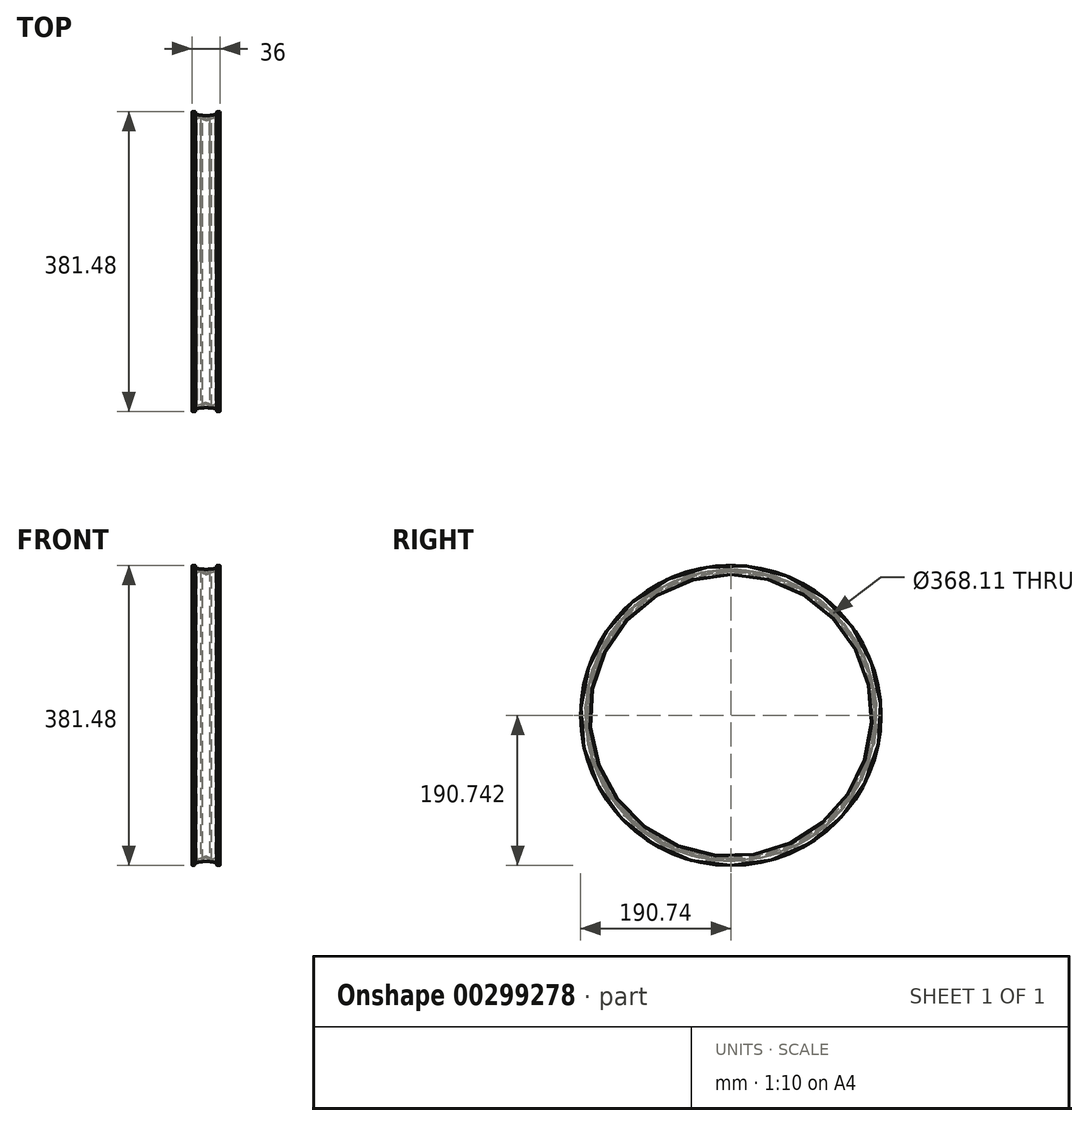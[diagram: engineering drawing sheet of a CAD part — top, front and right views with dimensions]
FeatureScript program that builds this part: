
annotation { "Feature Type Name" : "Feature", "Feature Type Description" : "" }
export const myFeature = defineFeature(function(context is Context, id is Id, definition is map)
    precondition{}
    {
        {
            var Q0;
            Q0=qCreatedBy(makeId("Front.planeOp"),FACE);
            var sketch = newSketch(context, id + "F0", { "sketchPlane" : qUnion([Q0])});
            skLineSegment(sketch, "E0", {"start": v(-18, 0) * mm, "end": v(-18, 12) * mm});
            skPoint(sketch, "E1", {"position": v(-14.7, 0) * mm});
            skPoint(sketch, "E2", {"position": v(-14.7, 2.3) * mm});
            skArc(sketch, "E3", {"start": v(-14.7, 0) * mm, "mid": v(-13.4, 1.15) * mm, "end": v(-14.7, 2.3) * mm});
            skLineSegment(sketch, "E4", {"start": v(-14.7, 2.3) * mm, "end": v(-14.7, 3.3) * mm});
            skLineSegment(sketch, "E5", {"start": v(-18, 12) * mm, "end": v(-9, 8.18) * mm});
            skLineSegment(sketch, "E6", {"start": v(-9, 8.18) * mm, "end": v(0, 12) * mm});
            skPoint(sketch, "E7", {"position": v(-14.7, 4.05) * mm});
            skLineSegment(sketch, "E8", {"start": v(-14.7, 4.05) * mm, "end": v(-14.7, 5.73) * mm});
            skLineSegment(sketch, "E9", {"start": v(-14.7, 5.73) * mm, "end": v(-0.65, 5.73) * mm});
            skLineSegment(sketch, "E10", {"start": v(-0.65, 5.73) * mm, "end": v(-14.7, 4.05) * mm});
            skPoint(sketch, "E11", {"position": v(0, 5.73) * mm});
            skLineSegment(sketch, "E12", {"start": v(-14.7, 6.73) * mm, "end": v(-14.7, 8.43) * mm});
            skLineSegment(sketch, "E13", {"start": v(-14.7, 8.43) * mm, "end": v(-10.58, 6.68) * mm});
            skLineSegment(sketch, "E14", {"start": v(-14.7, 6.73) * mm, "end": v(-10.58, 6.68) * mm});
            skPoint(sketch, "E15", {"position": v(0, 9.94) * mm});
            skLineSegment(sketch, "E16", {"start": v(0, 9.94) * mm, "end": v(-7.68, 6.68) * mm});
            skLineSegment(sketch, "E17", {"start": v(-7.68, 6.68) * mm, "end": v(0, 6.68) * mm});
            skLineSegment(sketch, "E18.MirrorCS", {"start": v(9, 8.18) * mm, "end": v(0, 12) * mm});
            skLineSegment(sketch, "E19.MirrorCS", {"start": v(0, 9.94) * mm, "end": v(7.68, 6.68) * mm});
            skLineSegment(sketch, "E20.MirrorCS", {"start": v(7.68, 6.68) * mm, "end": v(0, 6.68) * mm});
            skLineSegment(sketch, "E21.MirrorCS", {"start": v(0.65, 5.73) * mm, "end": v(14.7, 4.05) * mm});
            skLineSegment(sketch, "E22.MirrorCS", {"start": v(14.7, 4.05) * mm, "end": v(14.7, 5.73) * mm});
            skLineSegment(sketch, "E23.MirrorCS", {"start": v(18, 0) * mm, "end": v(18, 12) * mm});
            skArc(sketch, "E24.MirrorCS", {"start": v(14.7, 0) * mm, "mid": v(13.41, 1.15) * mm, "end": v(14.7, 2.3) * mm});
            skLineSegment(sketch, "E25.MirrorCS", {"start": v(14.7, 2.3) * mm, "end": v(14.7, 3.3) * mm});
            skLineSegment(sketch, "E26.MirrorCS", {"start": v(18, 12) * mm, "end": v(9, 8.18) * mm});
            skLineSegment(sketch, "E27", {"start": v(-18, 0) * mm, "end": v(-14.7, 0) * mm});
            skLineSegment(sketch, "E28", {"start": v(18, 0) * mm, "end": v(14.7, 0) * mm});
            skLineSegment(sketch, "E29.MirrorCS", {"start": v(14.7, 6.73) * mm, "end": v(10.58, 6.68) * mm});
            skLineSegment(sketch, "E30.MirrorCS", {"start": v(14.7, 6.73) * mm, "end": v(14.7, 8.43) * mm});
            skLineSegment(sketch, "E31.MirrorCS", {"start": v(14.7, 8.43) * mm, "end": v(10.58, 6.68) * mm});
            skArc(sketch, "E32", {"start": v(14.7, 3.3) * mm, "mid": v(0, 5.1) * mm, "end": v(-14.7, 3.3) * mm});
            skPoint(sketch, "E33", {"position": v(0, 2.3) * mm});
            skLineSegment(sketch, "E34", {"start": v(0, 2.3) * mm, "end": v(0, 190.73) * mm, "construction": true});
            skLineSegment(sketch, "E35", {"start": v(0, 190.73) * mm, "end": v(86.7, 190.73) * mm, "construction": true});
            skLineSegment(sketch, "E36", {"start": v(0.65, 5.73) * mm, "end": v(14.7, 5.73) * mm});
            skSolve(sketch);
        }
        {
            var Q0;
            Q0=makeQuery(id+"F0.imprint","IMPRINT",FACE,{"disambiguationData":[TD([[makeQuery(id+"F0.imprint","IMPRINT",EDGE,{"derivedFrom":sQuery(id+"F0.wireOp",EDGE,"E0")}),-1.0]])]});
            var Q1;
            Q1=sQuery(id+"F0.wireOp",EDGE,"E35");
            revolve(context, id + "F1", {"entities" : qUnion([Q0]), "axis" : qUnion([Q1]), "revolveType" : RevolveType.ONE_DIRECTION, "oppositeDirection" : true, "angle" : 360 * degree});
        }
        {
            var Q0;
            Q0=makeQuery(id+"F1.opRevolve","SWEPT_EDGE",EDGE,{"disambiguationData":[OSD([sQuery(id+"F0.wireOp",EDGE,"E23.MirrorCS"),sQuery(id+"F0.wireOp",EDGE,"E26.MirrorCS")])]});
            var Q1;
            Q1=makeQuery(id+"F1.opRevolve","SWEPT_EDGE",EDGE,{"disambiguationData":[OSD([sQuery(id+"F0.wireOp",EDGE,"E6"),sQuery(id+"F0.wireOp",EDGE,"E18.MirrorCS")])]});
            var Q2;
            Q2=makeQuery(id+"F1.opRevolve","SWEPT_EDGE",EDGE,{"disambiguationData":[OSD([sQuery(id+"F0.wireOp",EDGE,"E0"),sQuery(id+"F0.wireOp",EDGE,"E5")])]});
            fillet(context, id + "F2", {"entities" : qUnion([Q0, Q1, Q2]), "radius" : 1 * mm, "tangentPropagation" : true, "allowEdgeOverflow" : false});
        }
        {
            var Q0;
            Q0=makeQuery(id+"F1.opRevolve","SWEPT_EDGE",EDGE,{"disambiguationData":[OSD([sQuery(id+"F0.wireOp",EDGE,"E18.MirrorCS"),sQuery(id+"F0.wireOp",EDGE,"E26.MirrorCS")])]});
            var Q1;
            Q1=makeQuery(id+"F1.opRevolve","SWEPT_EDGE",EDGE,{"disambiguationData":[OSD([sQuery(id+"F0.wireOp",EDGE,"E5"),sQuery(id+"F0.wireOp",EDGE,"E6")])]});
            fillet(context, id + "F3", {"entities" : qUnion([Q0, Q1]), "radius" : 1 * mm, "tangentPropagation" : true, "allowEdgeOverflow" : false});
        }
        {
            var Q0;
            Q0=makeQuery(id+"F1.opRevolve","SWEPT_EDGE",EDGE,{"disambiguationData":[OSD([sQuery(id+"F0.wireOp",EDGE,"E29.MirrorCS"),sQuery(id+"F0.wireOp",EDGE,"E30.MirrorCS")])]});
            var Q1;
            Q1=makeQuery(id+"F1.opRevolve","SWEPT_EDGE",EDGE,{"disambiguationData":[OSD([sQuery(id+"F0.wireOp",EDGE,"E30.MirrorCS"),sQuery(id+"F0.wireOp",EDGE,"E31.MirrorCS")])]});
            var Q2;
            Q2=makeQuery(id+"F1.opRevolve","SWEPT_EDGE",EDGE,{"disambiguationData":[OSD([sQuery(id+"F0.wireOp",EDGE,"E29.MirrorCS"),sQuery(id+"F0.wireOp",EDGE,"E31.MirrorCS")])]});
            var Q3;
            Q3=makeQuery(id+"F1.opRevolve","SWEPT_EDGE",EDGE,{"disambiguationData":[OSD([sQuery(id+"F0.wireOp",EDGE,"E13"),sQuery(id+"F0.wireOp",EDGE,"E14")])]});
            var Q4;
            Q4=makeQuery(id+"F1.opRevolve","SWEPT_EDGE",EDGE,{"disambiguationData":[OSD([sQuery(id+"F0.wireOp",EDGE,"E12"),sQuery(id+"F0.wireOp",EDGE,"E13")])]});
            var Q5;
            Q5=makeQuery(id+"F1.opRevolve","SWEPT_EDGE",EDGE,{"disambiguationData":[OSD([sQuery(id+"F0.wireOp",EDGE,"E12"),sQuery(id+"F0.wireOp",EDGE,"E14")])]});
            fillet(context, id + "F4", {"entities" : qUnion([Q0, Q1, Q2, Q3, Q4, Q5]), "radius" : .25 * mm, "tangentPropagation" : true, "allowEdgeOverflow" : false});
        }
        {
            var Q0;
            Q0=makeQuery(id+"F1.opRevolve","SWEPT_EDGE",EDGE,{"disambiguationData":[OSD([sQuery(id+"F0.wireOp",EDGE,"E16"),sQuery(id+"F0.wireOp",EDGE,"E19.MirrorCS")])]});
            var Q1;
            Q1=makeQuery(id+"F1.opRevolve","SWEPT_EDGE",EDGE,{"disambiguationData":[OSD([sQuery(id+"F0.wireOp",EDGE,"E19.MirrorCS"),sQuery(id+"F0.wireOp",EDGE,"E20.MirrorCS")])]});
            var Q2;
            Q2=makeQuery(id+"F1.opRevolve","SWEPT_EDGE",EDGE,{"disambiguationData":[OSD([sQuery(id+"F0.wireOp",EDGE,"E16"),sQuery(id+"F0.wireOp",EDGE,"E17")])]});
            fillet(context, id + "F5", {"entities" : qUnion([Q0, Q1, Q2]), "radius" : .25 * mm, "tangentPropagation" : true, "allowEdgeOverflow" : false});
        }
        {
            var Q0;
            Q0=makeQuery(id+"F1.opRevolve","SWEPT_EDGE",EDGE,{"disambiguationData":[OSD([sQuery(id+"F0.wireOp",EDGE,"E22.MirrorCS"),sQuery(id+"F0.wireOp",EDGE,"E36")])]});
            var Q1;
            Q1=makeQuery(id+"F1.opRevolve","SWEPT_EDGE",EDGE,{"disambiguationData":[OSD([sQuery(id+"F0.wireOp",EDGE,"E21.MirrorCS"),sQuery(id+"F0.wireOp",EDGE,"E36")])]});
            var Q2;
            Q2=makeQuery(id+"F1.opRevolve","SWEPT_EDGE",EDGE,{"disambiguationData":[OSD([sQuery(id+"F0.wireOp",EDGE,"E21.MirrorCS"),sQuery(id+"F0.wireOp",EDGE,"E22.MirrorCS")])]});
            var Q3;
            Q3=makeQuery(id+"F1.opRevolve","SWEPT_EDGE",EDGE,{"disambiguationData":[OSD([sQuery(id+"F0.wireOp",EDGE,"E9"),sQuery(id+"F0.wireOp",EDGE,"E10")])]});
            var Q4;
            Q4=makeQuery(id+"F1.opRevolve","SWEPT_EDGE",EDGE,{"disambiguationData":[OSD([sQuery(id+"F0.wireOp",EDGE,"E8"),sQuery(id+"F0.wireOp",EDGE,"E9")])]});
            var Q5;
            Q5=makeQuery(id+"F1.opRevolve","SWEPT_EDGE",EDGE,{"disambiguationData":[OSD([sQuery(id+"F0.wireOp",EDGE,"E8"),sQuery(id+"F0.wireOp",EDGE,"E10")])]});
            fillet(context, id + "F6", {"entities" : qUnion([Q0, Q1, Q2, Q3, Q4, Q5]), "radius" : .25 * mm, "tangentPropagation" : true, "allowEdgeOverflow" : false});
        }
        {
            var Q0;
            Q0=makeQuery(id+"F1.opRevolve","SWEPT_EDGE",EDGE,{"disambiguationData":[OSD([sQuery(id+"F0.wireOp",EDGE,"E4"),sQuery(id+"F0.wireOp",EDGE,"E32")])]});
            var Q1;
            Q1=makeQuery(id+"F1.opRevolve","SWEPT_EDGE",EDGE,{"disambiguationData":[OSD([sQuery(id+"F0.wireOp",EDGE,"E3"),sQuery(id+"F0.wireOp",EDGE,"E4")])]});
            var Q2;
            Q2=makeQuery(id+"F1.opRevolve","SWEPT_EDGE",EDGE,{"disambiguationData":[OSD([sQuery(id+"F0.wireOp",EDGE,"E25.MirrorCS"),sQuery(id+"F0.wireOp",EDGE,"E32")])]});
            var Q3;
            Q3=makeQuery(id+"F1.opRevolve","SWEPT_EDGE",EDGE,{"disambiguationData":[OSD([sQuery(id+"F0.wireOp",EDGE,"E24.MirrorCS"),sQuery(id+"F0.wireOp",EDGE,"E25.MirrorCS")])]});
            fillet(context, id + "F7", {"entities" : qUnion([Q0, Q1, Q2, Q3]), "radius" : .5 * mm, "tangentPropagation" : true, "allowEdgeOverflow" : false});
        }
        {
            var Q0;
            Q0=makeQuery(id+"F1.opRevolve","SWEPT_EDGE",EDGE,{"disambiguationData":[OSD([sQuery(id+"F0.wireOp",EDGE,"E23.MirrorCS"),sQuery(id+"F0.wireOp",EDGE,"E28")])]});
            var Q1;
            Q1=makeQuery(id+"F1.opRevolve","SWEPT_EDGE",EDGE,{"disambiguationData":[OSD([sQuery(id+"F0.wireOp",EDGE,"E0"),sQuery(id+"F0.wireOp",EDGE,"E27")])]});
            fillet(context, id + "F8", {"entities" : qUnion([Q0, Q1]), "radius" : 1 * mm, "tangentPropagation" : true, "allowEdgeOverflow" : false});
        }
    });
